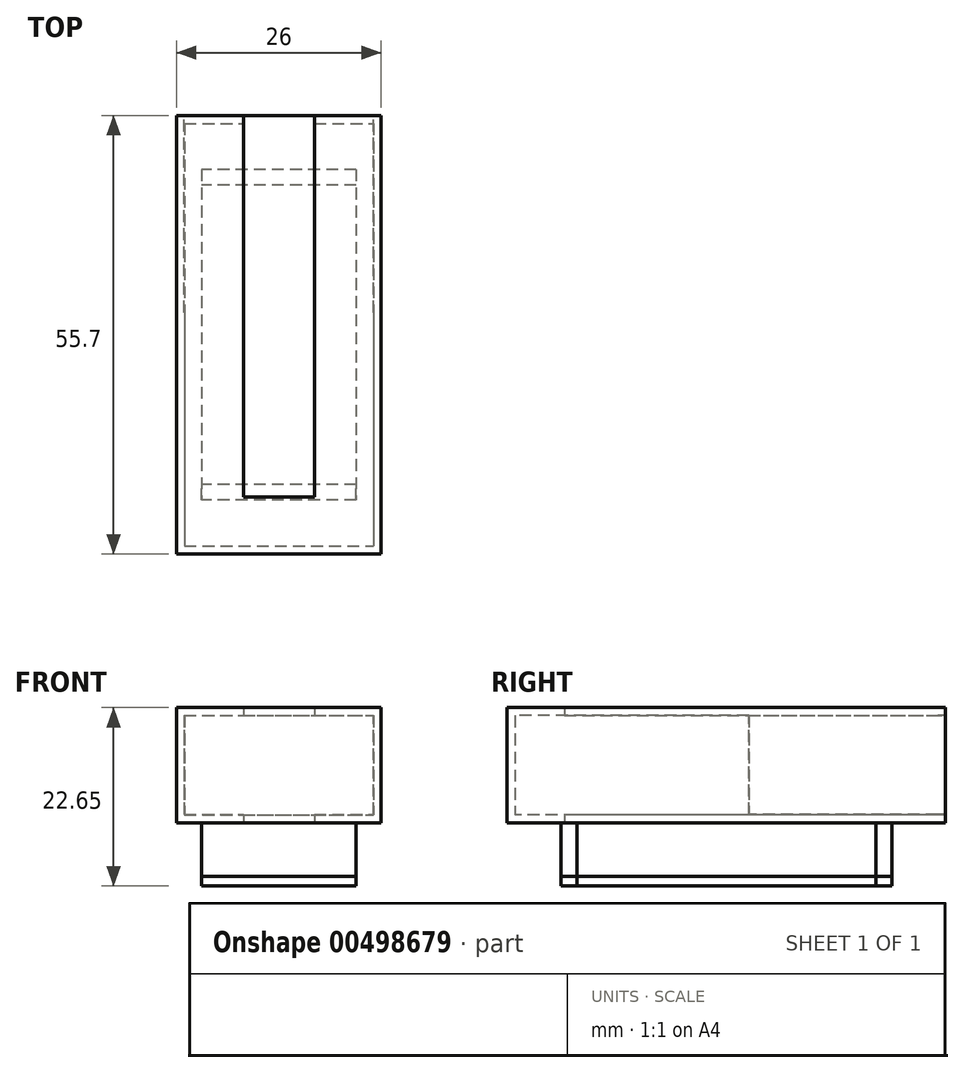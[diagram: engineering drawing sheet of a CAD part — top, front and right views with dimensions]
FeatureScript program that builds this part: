
annotation { "Feature Type Name" : "Feature", "Feature Type Description" : "" }
export const myFeature = defineFeature(function(context is Context, id is Id, definition is map)
    precondition{}
    {
        {
            var Q0;
            Q0=qCreatedBy(makeId("Top.planeOp"),FACE);
            var sketch = newSketch(context, id + "F0", { "sketchPlane" : qUnion([Q0])});
            skLineSegment(sketch, "E0.bottom", {"start": v(-13, 27.85) * mm, "end": v(-4.5, 27.85) * mm});
            skLineSegment(sketch, "E0.top", {"start": v(-13, -27.84) * mm, "end": v(13, -27.84) * mm});
            skLineSegment(sketch, "E0.left", {"start": v(-13, 27.85) * mm, "end": v(-13, -27.84) * mm});
            skLineSegment(sketch, "E0.right", {"start": v(13, 27.85) * mm, "end": v(13, -27.84) * mm});
            skPoint(sketch, "E0.middle", {"position": v(0, 0) * mm});
            skLineSegment(sketch, "E1.top", {"start": v(-4.5, -20.58) * mm, "end": v(4.5, -20.58) * mm});
            skLineSegment(sketch, "E1.left", {"start": v(-4.5, 27.84) * mm, "end": v(-4.5, -20.58) * mm});
            skLineSegment(sketch, "E1.right", {"start": v(4.5, 27.84) * mm, "end": v(4.5, -20.58) * mm});
            skLineSegment(sketch, "E2.trimOffspring", {"start": v(4.5, 27.85) * mm, "end": v(13, 27.85) * mm});
            skSolve(sketch);
        }
        {
            var Q0;
            Q0 = qSketchRegion(id + "F0", true);
            extrude(context, id + "F1", {"entities" : qUnion([Q0]), "depth" : 14.65 * mm});
        }
        {
            var Q0;
            Q0=makeQuery(id+"F1.opExtrude","SWEPT_FACE",FACE,{"disambiguationData":[OSD([sQuery(id+"F0.wireOp",EDGE,"E1.left")])]});
            var Q1;
            Q1=makeQuery(id+"F1.opExtrude","SWEPT_FACE",FACE,{"disambiguationData":[OSD([sQuery(id+"F0.wireOp",EDGE,"E1.right")])]});
            var Q2;
            Q2=makeQuery(id+"F1.opExtrude","SWEPT_FACE",FACE,{"disambiguationData":[OSD([sQuery(id+"F0.wireOp",EDGE,"E1.top")])]});
            shell(context, id + "F2", {"entities" : qUnion([Q0, Q1, Q2]), "thickness" : 1 * mm});
        }
        {
            var Q0;
            Q0=makeQuery(id+"F1.opExtrude","SWEPT_FACE",FACE,{"disambiguationData":[OSD([sQuery(id+"F0.wireOp",EDGE,"E0.bottom")])]});
            var sketch = newSketch(context, id + "F3", { "sketchPlane" : qUnion([Q0])});
            skLineSegment(sketch, "E3.bottom", {"start": v(12.07, 13.65) * mm, "end": v(-12.04, 13.65) * mm});
            skLineSegment(sketch, "E3.top", {"start": v(12.07, 1.08) * mm, "end": v(-12.04, 1.08) * mm});
            skLineSegment(sketch, "E3.left", {"start": v(12.07, 13.65) * mm, "end": v(12.07, 1.08) * mm});
            skLineSegment(sketch, "E3.right", {"start": v(-12.04, 13.65) * mm, "end": v(-12.04, 1.08) * mm});
            skSolve(sketch);
        }
        {
            var Q0;
            {var subQ0=sQuery(id+"F3.wireOp",EDGE,"E3.left");Q0=makeQuery(id+"F3.imprint","IMPRINT",FACE,{"disambiguationData":[TD([[makeQuery(id+"F3.imprint","IMPRINT",EDGE,{"derivedFrom":subQ0}),-1.0]])]});}
            var Q1;
            {var subQ0=sQuery(id+"F3.wireOp",EDGE,"E3.right");Q1=makeQuery(id+"F3.imprint","IMPRINT",FACE,{"disambiguationData":[TD([[makeQuery(id+"F3.imprint","IMPRINT",EDGE,{"derivedFrom":subQ0}),1.0]])]});}
            extrude(context, id + "F4", {"entities" : qUnion([Q0, Q1]), "operationType" : NewBodyOperationType.REMOVE, "oppositeDirection" : true, "depth" : 25 * mm});
        }
        {
            var Q0;
            Q0=makeQuery(id+"F1.opExtrude","CAP_FACE",FACE,{"disambiguationData":[OSD([sQuery(id+"F0.wireOp",EDGE,"E0.bottom"),sQuery(id+"F0.wireOp",EDGE,"E0.top"),sQuery(id+"F0.wireOp",EDGE,"E0.left"),sQuery(id+"F0.wireOp",EDGE,"E0.right"),sQuery(id+"F0.wireOp",EDGE,"E1.top"),sQuery(id+"F0.wireOp",EDGE,"E1.left"),sQuery(id+"F0.wireOp",EDGE,"E1.right"),sQuery(id+"F0.wireOp",EDGE,"E2.trimOffspring")])],"isStart":true});
            var sketch = newSketch(context, id + "F5", { "sketchPlane" : qUnion([Q0])});
            skLineSegment(sketch, "E4.bottom", {"start": v(13, -27.85) * mm, "end": v(-13, -27.85) * mm});
            skLineSegment(sketch, "E4.top", {"start": v(13, 27.85) * mm, "end": v(-13, 27.85) * mm});
            skLineSegment(sketch, "E4.left", {"start": v(13, -27.85) * mm, "end": v(13, 27.85) * mm});
            skLineSegment(sketch, "E4.right", {"start": v(-13, -27.85) * mm, "end": v(-13, 27.85) * mm});
            skPoint(sketch, "E4.middle", {"position": v(0, 0) * mm});
            skSolve(sketch);
        }
        {
            var Q0;
            Q0=makeQuery(id+"F5.imprint","IMPRINT",FACE,{"disambiguationData":[TD([[makeQuery(id+"F5.imprint","IMPRINT",EDGE,{"derivedFrom":makeQuery(id+"F1.opExtrude","CAP_EDGE",EDGE,{"disambiguationData":[OSD([sQuery(id+"F0.wireOp",EDGE,"E1.top")])],"isStart":true})}),-1.0]])]});
            extrude(context, id + "F6", {"entities" : qUnion([Q0]), "oppositeDirection" : true, "depth" : 1 * mm});
        }
        {
            var Q0;
            Q0=makeQuery(id+"F1.opExtrude","CAP_FACE",FACE,{"disambiguationData":[OSD([sQuery(id+"F0.wireOp",EDGE,"E0.bottom"),sQuery(id+"F0.wireOp",EDGE,"E0.top"),sQuery(id+"F0.wireOp",EDGE,"E0.left"),sQuery(id+"F0.wireOp",EDGE,"E0.right"),sQuery(id+"F0.wireOp",EDGE,"E1.top"),sQuery(id+"F0.wireOp",EDGE,"E1.left"),sQuery(id+"F0.wireOp",EDGE,"E1.right"),sQuery(id+"F0.wireOp",EDGE,"E2.trimOffspring")])],"isStart":true});
            var sketch = newSketch(context, id + "F7", { "sketchPlane" : qUnion([Q0])});
            skLineSegment(sketch, "E5", {"start": v(19.39, 0) * mm, "end": v(-21.34, 0) * mm, "construction": true});
            skPoint(sketch, "E5.endSnap0", {"position": v(13, 0) * mm});
            skLineSegment(sketch, "E6.bottom", {"start": v(9.82, -21) * mm, "end": v(-9.82, -21) * mm});
            skLineSegment(sketch, "E6.top", {"start": v(9.82, -19) * mm, "end": v(-9.82, -19) * mm});
            skLineSegment(sketch, "E6.left", {"start": v(9.82, -21) * mm, "end": v(9.82, -19) * mm});
            skLineSegment(sketch, "E6.right", {"start": v(-9.82, -21) * mm, "end": v(-9.82, -19) * mm});
            skPoint(sketch, "E6.middle", {"position": v(0, -20) * mm});
            skLineSegment(sketch, "E7.MirrorCS", {"start": v(9.82, 19) * mm, "end": v(-9.82, 19) * mm});
            skLineSegment(sketch, "E8.MirrorCS", {"start": v(9.82, 21) * mm, "end": v(9.82, 19) * mm});
            skLineSegment(sketch, "E9.MirrorCS", {"start": v(9.82, 21) * mm, "end": v(-9.82, 21) * mm});
            skLineSegment(sketch, "E10.MirrorCS", {"start": v(-9.82, 21) * mm, "end": v(-9.82, 19) * mm});
            skSolve(sketch);
        }
        {
            var Q0;
            {var subQ0=sQuery(id+"F7.wireOp",EDGE,"E6.left");Q0=makeQuery(id+"F7.imprint","IMPRINT",FACE,{"disambiguationData":[TD([[makeQuery(id+"F7.imprint","IMPRINT",EDGE,{"derivedFrom":subQ0}),1.0]])]});}
            var Q1;
            {var subQ0=sQuery(id+"F7.wireOp",EDGE,"E6.bottom");var subQ1=makeQuery(id+"F1.opExtrude","CAP_EDGE",EDGE,{"disambiguationData":[OSD([sQuery(id+"F0.wireOp",EDGE,"E1.right")])],"isStart":true});var subQ2=makeQuery(id+"F7.imprint","INTERSECT",VERTEX,{"derivedFrom":[subQ1,subQ0]});Q1=makeQuery(id+"F7.imprint","IMPRINT",FACE,{"disambiguationData":[TD([[makeQuery(id+"F7.imprint","IMPRINT",EDGE,{"disambiguationData":[TD([[subQ2,-1.0]])],"derivedFrom":subQ0}),-1.0]])]});}
            var Q2;
            {var subQ0=sQuery(id+"F7.wireOp",EDGE,"E6.right");Q2=makeQuery(id+"F7.imprint","IMPRINT",FACE,{"disambiguationData":[TD([[makeQuery(id+"F7.imprint","IMPRINT",EDGE,{"derivedFrom":subQ0}),-1.0]])]});}
            var Q3;
            {var subQ4=sQuery(id+"F7.wireOp",EDGE,"E8.MirrorCS");Q3=makeQuery(id+"F7.imprint","IMPRINT",FACE,{"disambiguationData":[TD([[makeQuery(id+"F7.imprint","IMPRINT",EDGE,{"derivedFrom":subQ4}),-1.0]])]});}
            var Q4;
            {var subQ5=makeQuery(id+"F1.opExtrude","CAP_EDGE",EDGE,{"disambiguationData":[OSD([sQuery(id+"F0.wireOp",EDGE,"E1.top")])],"isStart":true});Q4=makeQuery(id+"F7.imprint","IMPRINT",FACE,{"disambiguationData":[TD([[makeQuery(id+"F7.imprint","IMPRINT",EDGE,{"derivedFrom":subQ5}),-1.0]])]});}
            extrude(context, id + "F8", {"entities" : qUnion([Q0, Q1, Q2, Q3, Q4]), "depth" : 8 * mm});
        }
        {
            var Q0;
            Q0=makeQuery(id+"F8.opExtrude","CAP_FACE",FACE,{"disambiguationData":[OSD([sQuery(id+"F7.wireOp",EDGE,"E6.bottom"),sQuery(id+"F7.wireOp",EDGE,"E6.top"),sQuery(id+"F7.wireOp",EDGE,"E6.left"),sQuery(id+"F7.wireOp",EDGE,"E6.right")])],"isStart":false});
            var sketch = newSketch(context, id + "F9", { "sketchPlane" : qUnion([Q0])});
            skLineSegment(sketch, "E11.bottom", {"start": v(9.82, -21) * mm, "end": v(-9.82, -21) * mm});
            skLineSegment(sketch, "E11.top", {"start": v(9.82, 21) * mm, "end": v(-9.82, 21) * mm});
            skLineSegment(sketch, "E11.left", {"start": v(9.82, -21) * mm, "end": v(9.82, 21) * mm});
            skLineSegment(sketch, "E11.right", {"start": v(-9.82, -21) * mm, "end": v(-9.82, 21) * mm});
            skPoint(sketch, "E11.middle", {"position": v(0, 0) * mm});
            skSolve(sketch);
        }
        {
            var Q0;
            {var subQ0=sQuery(id+"F9.wireOp",EDGE,"E11.top");Q0=makeQuery(id+"F9.imprint","IMPRINT",FACE,{"disambiguationData":[TD([[makeQuery(id+"F9.imprint","IMPRINT",EDGE,{"derivedFrom":subQ0}),1.0]])]});}
            var Q1;
            {var subQ0=sQuery(id+"F9.wireOp",EDGE,"E11.bottom");Q1=makeQuery(id+"F9.imprint","IMPRINT",FACE,{"disambiguationData":[TD([[makeQuery(id+"F9.imprint","IMPRINT",EDGE,{"derivedFrom":subQ0}),-1.0]])]});}
            extrude(context, id + "F10", {"entities" : qUnion([Q0, Q1]), "oppositeDirection" : true, "depth" : 1.2 * mm});
        }
    });
